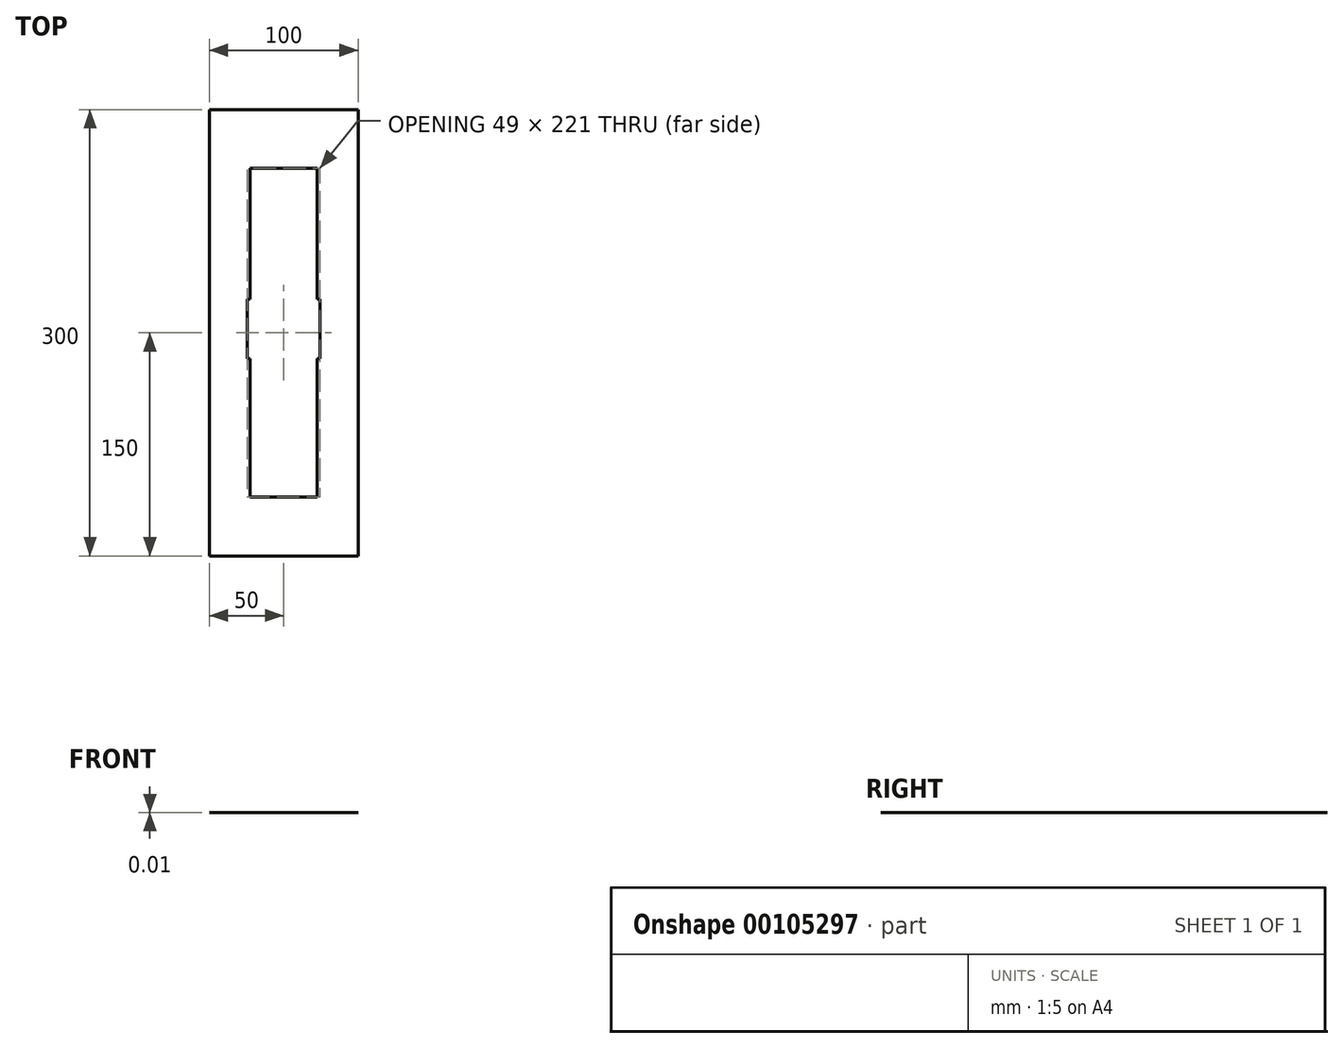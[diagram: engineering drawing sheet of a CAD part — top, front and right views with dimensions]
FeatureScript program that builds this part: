
annotation { "Feature Type Name" : "Feature", "Feature Type Description" : "" }
export const myFeature = defineFeature(function(context is Context, id is Id, definition is map)
    precondition{}
    {
        {
            var Q0;
            Q0=qCreatedBy(makeId("Top.planeOp"),FACE);
            var sketch = newSketch(context, id + "F0", { "sketchPlane" : qUnion([Q0])});
            skLineSegment(sketch, "E0.bottom", {"start": v(-50, -150) * mm, "end": v(50, -150) * mm});
            skLineSegment(sketch, "E0.top", {"start": v(-50, 150) * mm, "end": v(50, 150) * mm});
            skLineSegment(sketch, "E0.left", {"start": v(-50, -150) * mm, "end": v(-50, 150) * mm});
            skLineSegment(sketch, "E0.right", {"start": v(50, -150) * mm, "end": v(50, 150) * mm});
            skPoint(sketch, "E0.middle", {"position": v(0, 0) * mm});
            skSolve(sketch);
        }
        {
            var Q0;
            Q0=qSketchRegion(id+"F0",true);
            extrude(context, id + "F1", {"entities" : qUnion([Q0]), "depth" : 1 / 101.6 * mm});
        }
        {
            var Q0;
            Q0=makeQuery(id+"F1.opExtrude","CAP_FACE",FACE,{"disambiguationData":[OSD([sQuery(id+"F0.wireOp",EDGE,"E0.bottom"),sQuery(id+"F0.wireOp",EDGE,"E0.top"),sQuery(id+"F0.wireOp",EDGE,"E0.left"),sQuery(id+"F0.wireOp",EDGE,"E0.right")])],"isStart":false});
            var sketch = newSketch(context, id + "F2", { "sketchPlane" : qUnion([Q0])});
            skLineSegment(sketch, "E1.bottom", {"start": v(22.5, 110.5) * mm, "end": v(-22.5, 110.5) * mm});
            skLineSegment(sketch, "E1.top", {"start": v(22.5, -110.5) * mm, "end": v(-22.5, -110.5) * mm});
            skLineSegment(sketch, "E1.left", {"start": v(22.5, 110.5) * mm, "end": v(22.5, -110.5) * mm});
            skLineSegment(sketch, "E1.right", {"start": v(-22.5, 110.5) * mm, "end": v(-22.5, -110.5) * mm});
            skPoint(sketch, "E1.middle", {"position": v(0, 0) * mm});
            skLineSegment(sketch, "E2.bottom", {"start": v(22.5, -17.52) * mm, "end": v(24.5, -17.52) * mm});
            skLineSegment(sketch, "E2.top", {"start": v(22.5, 22.48) * mm, "end": v(24.5, 22.48) * mm});
            skLineSegment(sketch, "E2.left", {"start": v(22.5, -17.52) * mm, "end": v(22.5, 22.48) * mm});
            skLineSegment(sketch, "E2.right", {"start": v(24.5, -17.52) * mm, "end": v(24.5, 22.48) * mm});
            skLineSegment(sketch, "E3.bottom", {"start": v(-22.5, 22.48) * mm, "end": v(-24.5, 22.48) * mm});
            skLineSegment(sketch, "E3.top", {"start": v(-22.5, -17.52) * mm, "end": v(-24.5, -17.52) * mm});
            skLineSegment(sketch, "E3.left", {"start": v(-22.5, 22.48) * mm, "end": v(-22.5, -17.52) * mm});
            skLineSegment(sketch, "E3.right", {"start": v(-24.5, 22.48) * mm, "end": v(-24.5, -17.52) * mm});
            skSolve(sketch);
        }
        {
            var Q0;
            Q0=qSketchRegion(id+"F2",true);
            extrude(context, id + "F3", {"entities" : qUnion([Q0]), "operationType" : NewBodyOperationType.REMOVE, "oppositeDirection" : true, "depth" : 25.4 * mm});
        }
    });
